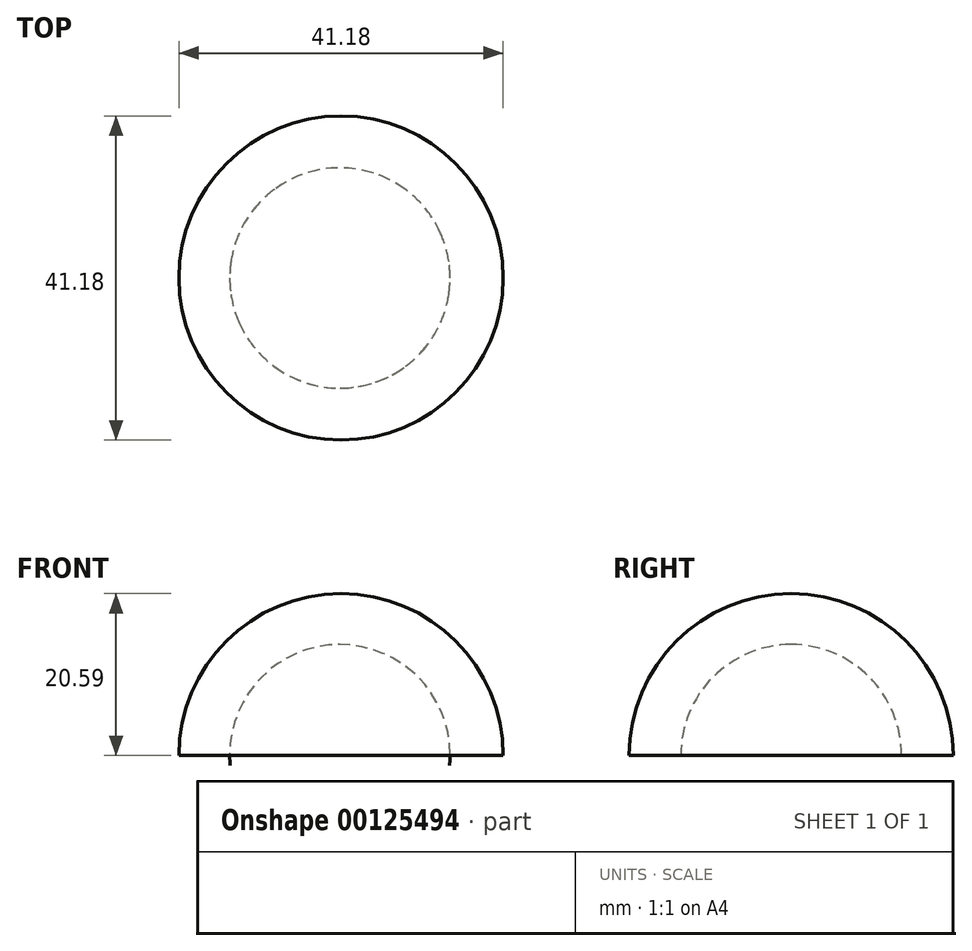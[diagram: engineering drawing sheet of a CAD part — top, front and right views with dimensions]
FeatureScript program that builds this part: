
annotation { "Feature Type Name" : "Feature", "Feature Type Description" : "" }
export const myFeature = defineFeature(function(context is Context, id is Id, definition is map)
    precondition{}
    {
        {
            var Q0;
            Q0=qCreatedBy(makeId("Front.planeOp"),FACE);
            var sketch = newSketch(context, id + "F0", { "sketchPlane" : qUnion([Q0])});
            skCircle(sketch, "E0", {"center": v(0, 0) * mm, "radius": 20.6 * mm});
            skLineSegment(sketch, "E1", {"start": v(0, 0) * mm, "end": v(-20.6, 0) * mm});
            skLineSegment(sketch, "E2", {"start": v(0, 0) * mm, "end": v(20.6, 0) * mm});
            skLineSegment(sketch, "E3", {"start": v(-20.6, 0) * mm, "end": v(-75.83, 0) * mm, "construction": true});
            skSolve(sketch);
        }
        {
            var Q0;
            {var subQ0=sQuery(id+"F0.wireOp",EDGE,"E1");Q0=makeQuery(id+"F0.imprint","IMPRINT",FACE,{"disambiguationData":[TD([[makeQuery(id+"F0.imprint","IMPRINT",EDGE,{"derivedFrom":subQ0}),-1.0]])]});}
            var Q1;
            Q1=sQuery(id+"F0.wireOp",EDGE,"E3");
            revolve(context, id + "F1", {"entities" : qUnion([Q0]), "axis" : qUnion([Q1]), "revolveType" : RevolveType.TWO_DIRECTIONS, "angle" : 90 * degree, "angleBack" : 270 * degree});
        }
        {
            var Q0;
            Q0=qCreatedBy(makeId("Front.planeOp"),FACE);
            var sketch = newSketch(context, id + "F2", { "sketchPlane" : qUnion([Q0])});
            skCircle(sketch, "E4", {"center": v(-0.15, 0.12) * mm, "radius": 14 * mm});
            skLineSegment(sketch, "E5", {"start": v(-0.15, 0.12) * mm, "end": v(-14.14, 0.12) * mm});
            skLineSegment(sketch, "E6", {"start": v(-0.15, 0.12) * mm, "end": v(13.85, 0.12) * mm});
            skLineSegment(sketch, "E7", {"start": v(-14.14, 0.12) * mm, "end": v(-120.66, 0.12) * mm, "construction": true});
            skSolve(sketch);
        }
        {
            var Q0;
            {var subQ0=sQuery(id+"F2.wireOp",EDGE,"E5");Q0=makeQuery(id+"F2.imprint","IMPRINT",FACE,{"disambiguationData":[TD([[makeQuery(id+"F2.imprint","IMPRINT",EDGE,{"derivedFrom":subQ0}),-1.0]])]});}
            var Q1;
            Q1=sQuery(id+"F2.wireOp",EDGE,"E7");
            revolve(context, id + "F3", {"operationType" : NewBodyOperationType.REMOVE, "entities" : qUnion([Q0]), "axis" : qUnion([Q1]), "revolveType" : RevolveType.FULL, "oppositeDirection" : true});
        }
    });
